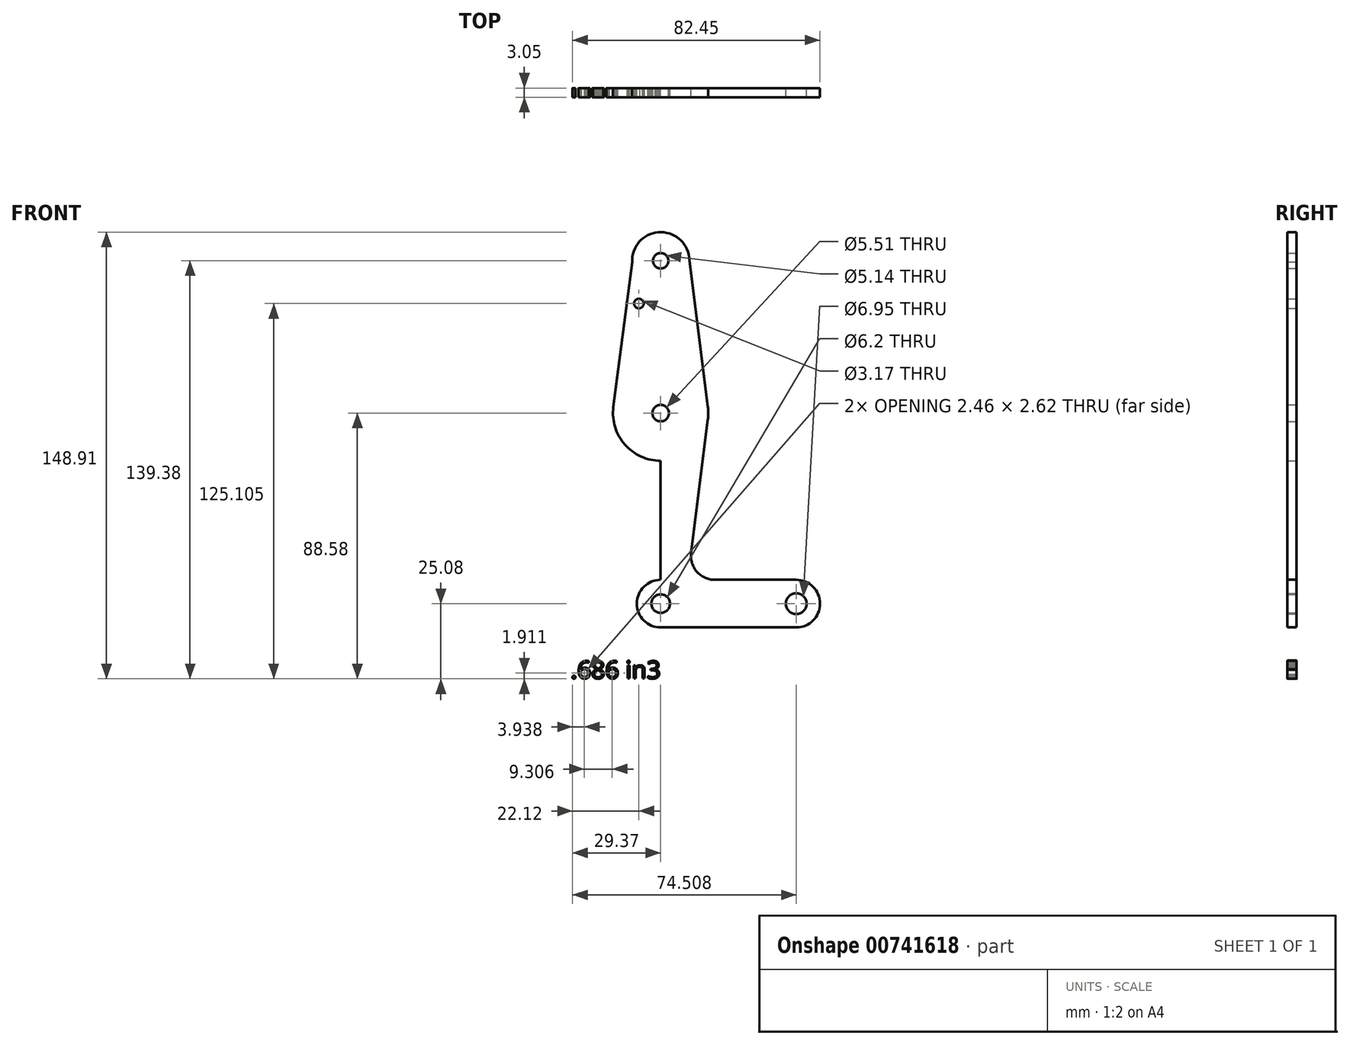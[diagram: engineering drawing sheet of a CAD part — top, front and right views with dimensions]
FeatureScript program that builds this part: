
annotation { "Feature Type Name" : "Feature", "Feature Type Description" : "" }
export const myFeature = defineFeature(function(context is Context, id is Id, definition is map)
    precondition{}
    {
        {
            var Q0;
            Q0=qCreatedBy(makeId("Front.planeOp"),FACE);
            var sketch = newSketch(context, id + "F0", { "sketchPlane" : qUnion([Q0])});
            skCircle(sketch, "E0", {"center": v(0, 0) * mm, "radius": 7.94 * mm});
            skCircle(sketch, "E1", {"center": v(45.14, 0) * mm, "radius": 7.94 * mm});
            skCircle(sketch, "E2", {"center": v(0, 114.3) * mm, "radius": 9.53 * mm});
            skLineSegment(sketch, "E3", {"start": v(0, 114.3) * mm, "end": v(0, 0) * mm});
            skLineSegment(sketch, "E4", {"start": v(0, 63.5) * mm, "end": v(0, 0) * mm});
            skLineSegment(sketch, "E5", {"start": v(10.13, 16.88) * mm, "end": v(15.75, 61.52) * mm});
            skLineSegment(sketch, "E6", {"start": v(15.75, 65.48) * mm, "end": v(9.45, 115.5) * mm});
            skLineSegment(sketch, "E7", {"start": v(0, 0) * mm, "end": v(45.14, 0) * mm});
            skLineSegment(sketch, "E8", {"start": v(18.01, 7.94) * mm, "end": v(45.14, 7.94) * mm});
            skLineSegment(sketch, "E9", {"start": v(0, -7.94) * mm, "end": v(45.14, -7.94) * mm});
            skCircle(sketch, "E10", {"center": v(-7.25, 100.03) * mm, "radius": 1.59 * mm});
            skPoint(sketch, "E11.newPointA", {"position": v(8, 0) * mm});
            skArc(sketch, "E11.filletArc", {"start": v(10.13, 16.88) * mm, "mid": v(12.05, 10.63) * mm, "end": v(18.01, 7.94) * mm});
            skCircle(sketch, "E12", {"center": v(0, 63.5) * mm, "radius": 15.88 * mm});
            skLineSegment(sketch, "E13", {"start": v(-9.52, 113.87) * mm, "end": v(-15.74, 65.53) * mm});
            skLineSegment(sketch, "E14", {"start": v(-7.94, 0) * mm, "end": v(-15.74, 61.47) * mm});
            skCircle(sketch, "E15", {"center": v(0, 0) * mm, "radius": 3.1 * mm});
            skCircle(sketch, "E16", {"center": v(45.14, 0) * mm, "radius": 3.47 * mm});
            skCircle(sketch, "E17", {"center": v(0, 63.5) * mm, "radius": 2.75 * mm});
            skCircle(sketch, "E18", {"center": v(0, 114.3) * mm, "radius": 2.57 * mm});
            skText(sketch, "E19", { "text": ".686 in3", "fontName": "OpenSans-Regular.ttf"});
            const initialGuessF0  = {"E19": [-0.02997, -0.02496, 1, 0, 0.00586]};
            skSetInitialGuess(sketch, initialGuessF0);
            skSolve(sketch);
        }
        {
            var Q0;
            Q0 = qSketchRegion(id + "F0", true);
            var Q1;
            {var subQ0=sQuery(id+"F0.wireOp",EDGE,"E4");var subQ1=sQuery(id+"F0.wireOp",EDGE,"E0");var subQ2=makeQuery(id+"F0.imprint","INTERSECT",VERTEX,{"derivedFrom":[subQ1,subQ0]});Q1=makeQuery(id+"F0.imprint","IMPRINT",FACE,{"disambiguationData":[TD([[makeQuery(id+"F0.imprint","IMPRINT",EDGE,{"disambiguationData":[TD([[subQ2,1.0]])],"derivedFrom":subQ1}),1.0]])]});}
            extrude(context, id + "F1", {"entities" : qUnion([Q0, Q1]), "depth" : 3.05 * mm, "offsetDistance" : 25.4 * mm});
        }
    });
